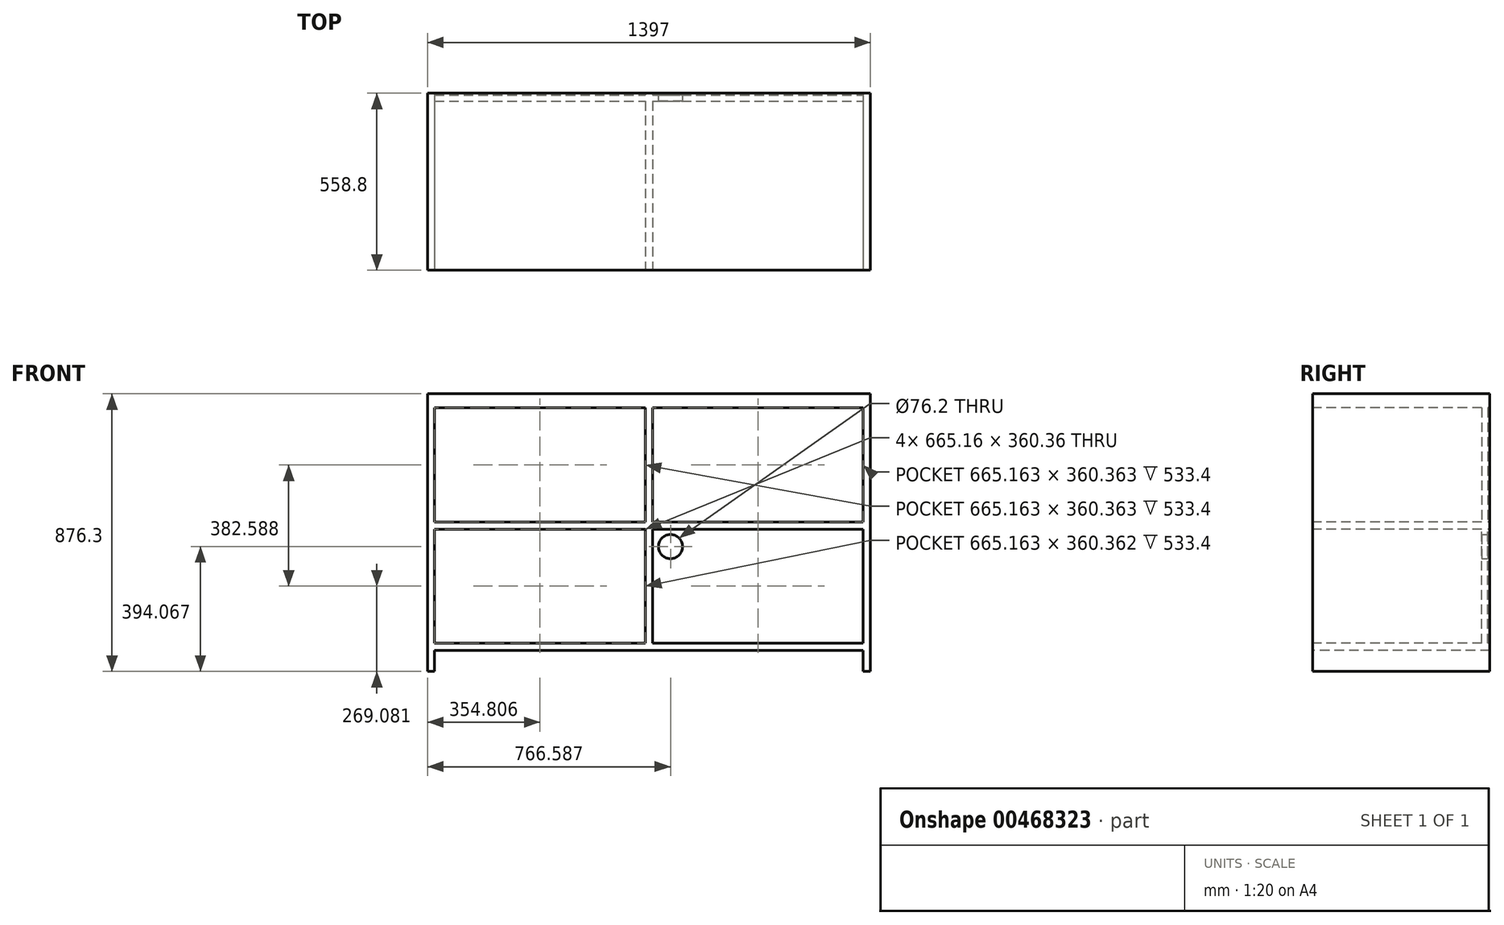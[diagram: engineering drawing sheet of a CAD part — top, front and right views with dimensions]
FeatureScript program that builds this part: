
annotation { "Feature Type Name" : "Feature", "Feature Type Description" : "" }
export const myFeature = defineFeature(function(context is Context, id is Id, definition is map)
    precondition{}
    {
        {
            var Q0;
            Q0=qCreatedBy(makeId("Front.planeOp"),FACE);
            var sketch = newSketch(context, id + "F0", { "sketchPlane" : qUnion([Q0])});
            skLineSegment(sketch, "E0.bottom", {"start": v(0, 0) * mm, "end": v(22.23, 0) * mm});
            skLineSegment(sketch, "E0.top", {"start": v(0, 876.3) * mm, "end": v(22.22, 876.3) * mm});
            skLineSegment(sketch, "E0.left", {"start": v(0, 0) * mm, "end": v(0, 876.3) * mm});
            skLineSegment(sketch, "E0.right", {"start": v(22.23, 0) * mm, "end": v(22.23, 66.68) * mm});
            skLineSegment(sketch, "E1.bottom", {"start": v(22.22, 876.3) * mm, "end": v(1374.77, 876.3) * mm});
            skLineSegment(sketch, "E1.top", {"start": v(22.22, 831.85) * mm, "end": v(687.39, 831.85) * mm});
            skLineSegment(sketch, "E2.bottom", {"start": v(1374.77, 876.3) * mm, "end": v(1397, 876.3) * mm});
            skLineSegment(sketch, "E2.top", {"start": v(1374.77, 0) * mm, "end": v(1397, 0) * mm});
            skLineSegment(sketch, "E2.left", {"start": v(1374.77, 831.85) * mm, "end": v(1374.77, 471.49) * mm});
            skLineSegment(sketch, "E2.right", {"start": v(1397, 876.3) * mm, "end": v(1397, 0) * mm});
            skLineSegment(sketch, "E3.bottom", {"start": v(22.23, 66.68) * mm, "end": v(1374.77, 66.68) * mm});
            skLineSegment(sketch, "E3.top", {"start": v(22.22, 88.9) * mm, "end": v(687.39, 88.9) * mm});
            skLineSegment(sketch, "E4.left", {"start": v(687.39, 88.9) * mm, "end": v(687.39, 449.26) * mm});
            skLineSegment(sketch, "E4.right", {"start": v(709.61, 88.9) * mm, "end": v(709.61, 449.26) * mm});
            skLineSegment(sketch, "E5", {"start": v(1374.78, 88.9) * mm, "end": v(1374.78, 449.26) * mm});
            skLineSegment(sketch, "E6.bottom", {"start": v(1374.78, 449.26) * mm, "end": v(709.61, 449.26) * mm});
            skLineSegment(sketch, "E6.top", {"start": v(1374.78, 471.49) * mm, "end": v(709.61, 471.49) * mm});
            skLineSegment(sketch, "E7.trimOffspring", {"start": v(687.39, 471.49) * mm, "end": v(22.22, 471.49) * mm});
            skLineSegment(sketch, "E8.trimOffspring", {"start": v(687.39, 449.26) * mm, "end": v(22.23, 449.26) * mm});
            skLineSegment(sketch, "E9.trimOffspring", {"start": v(687.39, 471.49) * mm, "end": v(687.39, 831.85) * mm});
            skLineSegment(sketch, "E10.trimOffspring", {"start": v(709.61, 471.49) * mm, "end": v(709.61, 831.85) * mm});
            skLineSegment(sketch, "E11.trimOffspring", {"start": v(22.23, 471.49) * mm, "end": v(22.23, 831.85) * mm});
            skLineSegment(sketch, "E12.trimOffspring", {"start": v(709.61, 831.85) * mm, "end": v(1374.77, 831.85) * mm});
            skLineSegment(sketch, "E13.trimOffspring", {"start": v(1374.77, 449.26) * mm, "end": v(1374.77, 88.9) * mm});
            skLineSegment(sketch, "E14.trimOffspring", {"start": v(1374.77, 66.68) * mm, "end": v(1374.77, 0) * mm});
            skLineSegment(sketch, "E15.trimOffspring", {"start": v(709.61, 88.9) * mm, "end": v(1374.78, 88.9) * mm});
            skLineSegment(sketch, "E16.trimOffspring", {"start": v(22.23, 88.9) * mm, "end": v(22.23, 449.26) * mm});
            skSolve(sketch);
        }
        {
            var Q0;
            Q0=makeQuery(id+"F0.imprint","IMPRINT",FACE,{"disambiguationData":[TD([[makeQuery(id+"F0.imprint","IMPRINT",EDGE,{"derivedFrom":sQuery(id+"F0.wireOp",EDGE,"E0.bottom")}),1.0]])]});
            extrude(context, id + "F1", {"entities" : qUnion([Q0]), "oppositeDirection" : true, "depth" : 558.8 * mm});
        }
        {
            var Q0;
            Q0=makeQuery(id+"F1.opExtrude","CAP_FACE",FACE,{"disambiguationData":[OSD([sQuery(id+"F0.wireOp",EDGE,"E0.bottom"),sQuery(id+"F0.wireOp",EDGE,"E0.top"),sQuery(id+"F0.wireOp",EDGE,"E0.left"),sQuery(id+"F0.wireOp",EDGE,"E1.bottom"),sQuery(id+"F0.wireOp",EDGE,"E1.top"),sQuery(id+"F0.wireOp",EDGE,"E2.bottom"),sQuery(id+"F0.wireOp",EDGE,"E2.top"),sQuery(id+"F0.wireOp",EDGE,"E2.left"),sQuery(id+"F0.wireOp",EDGE,"E2.right"),sQuery(id+"F0.wireOp",EDGE,"E0.right"),sQuery(id+"F0.wireOp",EDGE,"E3.bottom"),sQuery(id+"F0.wireOp",EDGE,"E3.top"),sQuery(id+"F0.wireOp",EDGE,"E4.left"),sQuery(id+"F0.wireOp",EDGE,"E4.right"),sQuery(id+"F0.wireOp",EDGE,"E6.bottom"),sQuery(id+"F0.wireOp",EDGE,"E6.top"),sQuery(id+"F0.wireOp",EDGE,"E7.trimOffspring"),sQuery(id+"F0.wireOp",EDGE,"E8.trimOffspring"),sQuery(id+"F0.wireOp",EDGE,"E9.trimOffspring"),sQuery(id+"F0.wireOp",EDGE,"E10.trimOffspring"),sQuery(id+"F0.wireOp",EDGE,"E11.trimOffspring"),sQuery(id+"F0.wireOp",EDGE,"E12.trimOffspring"),sQuery(id+"F0.wireOp",EDGE,"E13.trimOffspring"),sQuery(id+"F0.wireOp",EDGE,"E14.trimOffspring"),sQuery(id+"F0.wireOp",EDGE,"E15.trimOffspring"),sQuery(id+"F0.wireOp",EDGE,"E16.trimOffspring")])],"isStart":false});
            cPlane(context, id + "F2", {"entities" : qUnion([Q0]), "cplaneType" : CPlaneType.OFFSET, "offset" : 6.35 * mm, "oppositeDirection" : true, "width" : 152.4 * mm, "height" : 152.4 * mm});
        }
        {
            var Q0;
            Q0=qCreatedBy(id+"F2.planeOp",FACE);
            var sketch = newSketch(context, id + "F3", { "sketchPlane" : qUnion([Q0])});
            skLineSegment(sketch, "E17.bottom", {"start": v(-1389.06, 861.33) * mm, "end": v(-17.76, 861.33) * mm});
            skLineSegment(sketch, "E17.top", {"start": v(-1389.06, 80.42) * mm, "end": v(-17.76, 80.42) * mm});
            skLineSegment(sketch, "E17.left", {"start": v(-1389.06, 861.33) * mm, "end": v(-1389.06, 80.42) * mm});
            skLineSegment(sketch, "E17.right", {"start": v(-17.76, 861.33) * mm, "end": v(-17.76, 80.42) * mm});
            skCircle(sketch, "E18", {"center": v(-766.59, 394.07) * mm, "radius": 38.1 * mm});
            skSolve(sketch);
        }
        {
            var Q0;
            Q0 = qSketchRegion(id + "F3", true);
            extrude(context, id + "F4", {"entities" : qUnion([Q0]), "operationType" : NewBodyOperationType.ADD, "oppositeDirection" : true, "depth" : 19.05 * mm});
        }
    });
